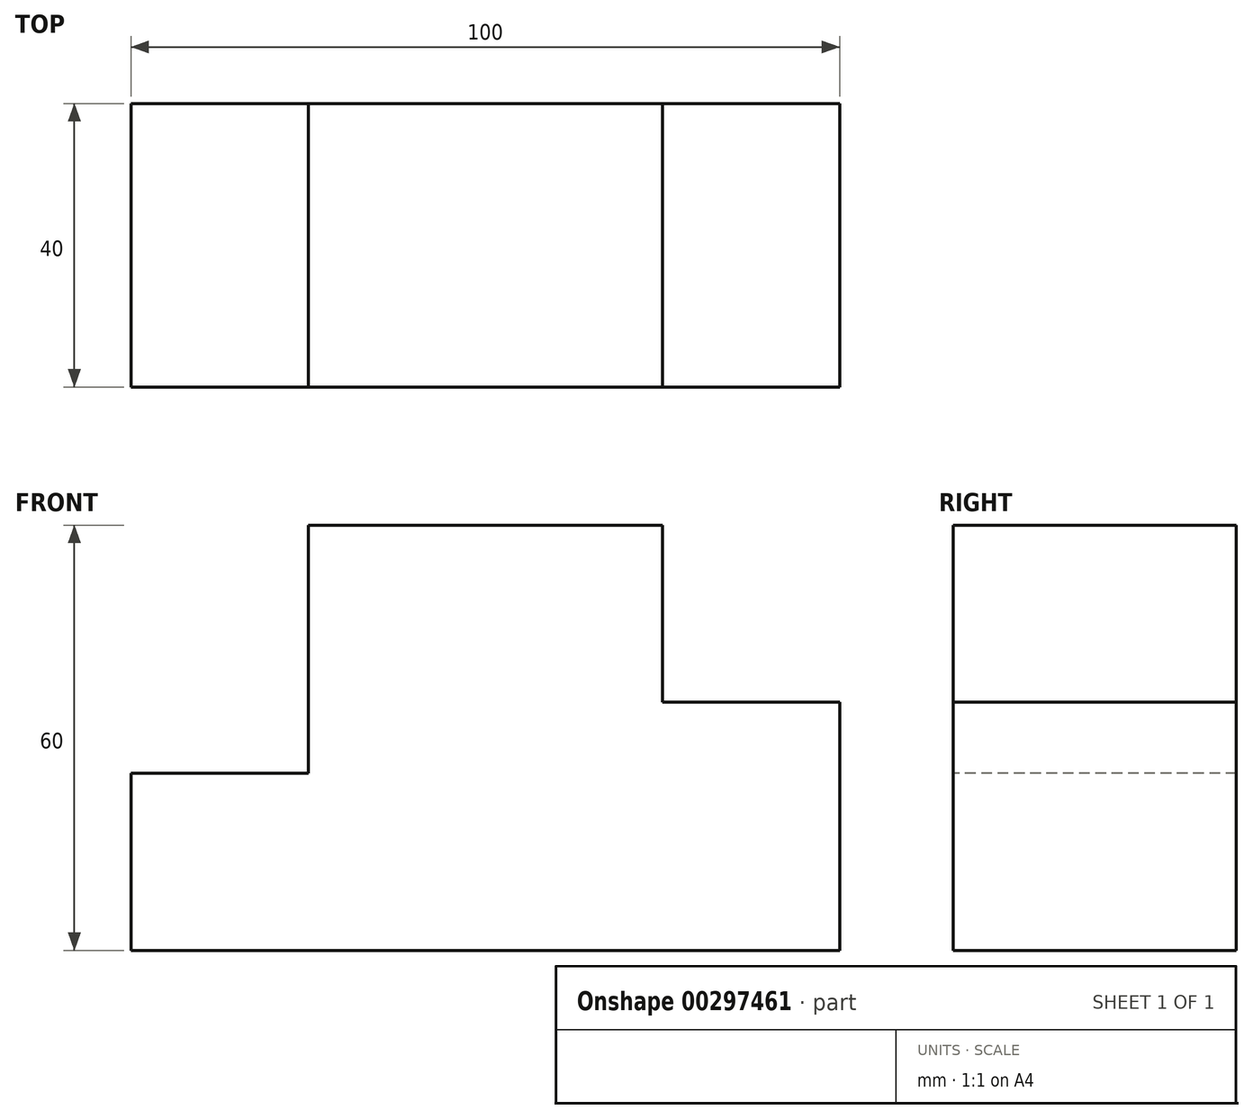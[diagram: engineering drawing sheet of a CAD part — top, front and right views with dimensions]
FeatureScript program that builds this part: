
annotation { "Feature Type Name" : "Feature", "Feature Type Description" : "" }
export const myFeature = defineFeature(function(context is Context, id is Id, definition is map)
    precondition{}
    {
        {
            var Q0;
            Q0=qCreatedBy(makeId("Front.planeOp"),FACE);
            var sketch = newSketch(context, id + "F0", { "sketchPlane" : qUnion([Q0])});
            skLineSegment(sketch, "E0.bottom", {"start": v(50, -30) * mm, "end": v(-50, -30) * mm});
            skLineSegment(sketch, "E0.top", {"start": v(50, 30) * mm, "end": v(-50, 30) * mm});
            skLineSegment(sketch, "E0.left", {"start": v(50, -30) * mm, "end": v(50, 30) * mm});
            skLineSegment(sketch, "E0.right", {"start": v(-50, -30) * mm, "end": v(-50, 30) * mm});
            skPoint(sketch, "E0.middle", {"position": v(0, 0) * mm});
            skSolve(sketch);
        }
        {
            var Q0;
            Q0 = qSketchRegion(id + "F0", true);
            extrude(context, id + "F1", {"entities" : qUnion([Q0]), "depth" : 40 * mm});
        }
        {
            var Q0;
            Q0=makeQuery(id+"F1.opExtrude","CAP_FACE",FACE,{"disambiguationData":[OSD([sQuery(id+"F0.wireOp",EDGE,"E0.bottom"),sQuery(id+"F0.wireOp",EDGE,"E0.top"),sQuery(id+"F0.wireOp",EDGE,"E0.left"),sQuery(id+"F0.wireOp",EDGE,"E0.right")])],"isStart":false});
            var sketch = newSketch(context, id + "F2", { "sketchPlane" : qUnion([Q0])});
            skLineSegment(sketch, "E1.bottom", {"start": v(-50, 30) * mm, "end": v(-25, 30) * mm});
            skLineSegment(sketch, "E1.top", {"start": v(-50, -5) * mm, "end": v(-25, -5) * mm});
            skLineSegment(sketch, "E1.left", {"start": v(-50, 30) * mm, "end": v(-50, -5) * mm});
            skLineSegment(sketch, "E1.right", {"start": v(-25, 30) * mm, "end": v(-25, -5) * mm});
            skSolve(sketch);
        }
        {
            var Q0;
            Q0=makeQuery(id+"F2.imprint","IMPRINT",FACE,{"disambiguationData":[TD([[makeQuery(id+"F2.imprint","IMPRINT",EDGE,{"derivedFrom":sQuery(id+"F2.wireOp",EDGE,"E1.bottom")}),1.0]])]});
            extrude(context, id + "F3", {"entities" : qUnion([Q0]), "operationType" : NewBodyOperationType.REMOVE, "oppositeDirection" : true, "depth" : 40 * mm});
        }
        {
            var Q0;
            Q0=makeQuery(id+"F1.opExtrude","CAP_FACE",FACE,{"disambiguationData":[OSD([sQuery(id+"F0.wireOp",EDGE,"E0.bottom"),sQuery(id+"F0.wireOp",EDGE,"E0.top"),sQuery(id+"F0.wireOp",EDGE,"E0.left"),sQuery(id+"F0.wireOp",EDGE,"E0.right")])],"isStart":false});
            var sketch = newSketch(context, id + "F4", { "sketchPlane" : qUnion([Q0])});
            skLineSegment(sketch, "E2.bottom", {"start": v(50, 30) * mm, "end": v(25, 30) * mm});
            skLineSegment(sketch, "E2.top", {"start": v(50, 5) * mm, "end": v(25, 5) * mm});
            skLineSegment(sketch, "E2.left", {"start": v(50, 30) * mm, "end": v(50, 5) * mm});
            skLineSegment(sketch, "E2.right", {"start": v(25, 30) * mm, "end": v(25, 5) * mm});
            skSolve(sketch);
        }
        {
            var Q0;
            Q0=makeQuery(id+"F4.imprint","IMPRINT",FACE,{"disambiguationData":[TD([[makeQuery(id+"F4.imprint","IMPRINT",EDGE,{"derivedFrom":sQuery(id+"F4.wireOp",EDGE,"E2.bottom")}),1.0]])]});
            extrude(context, id + "F5", {"entities" : qUnion([Q0]), "operationType" : NewBodyOperationType.REMOVE, "oppositeDirection" : true, "depth" : 40 * mm});
        }
    });
